# Revit family: NBS_Allermuir_OffcChrs-en-us-Cardita_SideChair
name_source: partatom
category: Furniture
revit_build: Autodesk Revit 2018 (Build: 20190510_1515(x64)
units: mm (PartAtom-declared; Revit-internal decimal feet)

## family parameters
Always vertical = Yes
Cut with Voids When Loaded = No
Room Calculation Point = No
Shared = No
Work Plane-Based = No

## types (1)
- Cardita_SideChair_CRD01
    AssetType = Movable
    BIMObjectName = NBS_Allermuir_OfficeChairs_Cardita_SideChair_CRD01-US
    Category = Pr_40_50_12_57:Office chairs
    ChairMaterial = NBS_Allermuir_Fabric
    Color = White as Snow, Back to Black, Slate Gray, Smoke Gray, Vintage Red, Ruby Red, Fern Green, Peacock Green
    Description = Side chair on wood legs
    DurationUnit = year
    ExpectedLife = 10
    Features = Molded shell, Fully upholstered with luxury quilt detail, Solid Ash legs with a clear finish, Plastic glides, Solid Ash legs can be stained or colorwashed, Plastic glides with felt
    Finish = White as Snow, Back to Black, Slate Gray, Smoke Gray, Vintage Red, Ruby Red, Fern Green, Peacock Green
    FrameFinish = Clear
    FrameMaterial = Solid Ash
    HighestSeatingHeight = 0 "
    IfcExportAs = IfcFurnitureType
    IfcExportType = CHAIR
    IsBuiltIn = No
    LegMaterial = NBS_Allermuir_Ash_ClearFinish
    LowestSeatingHeight = 0 "
    ManufacturerName = Allermuir
    ManufacturerURL = www.allermuir.com
    Material = Wood, steel
    ModelNumber = CRD01
    ModelReference = Cardita_SideChair
    NBSCertification = www.nationalbimlibrary.com/cert/rpltu2fz
    NBSDescription = Office chairs
    NBSReference = 45-35-20/330
    Name = OfficeChairs_CRD01_Cardita_Allermuir
    NominalDepth = 25 "
    NominalHeight = 33 "
    NominalLength = 22 "
    NominalWidth = 22 "
    OmniClassCode = 22-12 52 23
    OmniClassTitle = Office Seating
    OmniClassVersion = Table 22 2012-05-16
    ProductInformation = https://www.allermuir.com
    SeatDepth = 17.25"
    SeatWidth = 19"
    SeatingHeight = 17 "
    Size = 24.5 x 32.75 x 21.75"
    Status = UNSET
    Style = Chair
    SustainabilityPerformance = 99% recyclable
    Uniclass2015Code = Pr_40_50_12_57
    Uniclass2015Title = Office chairs
    Uniclass2015Version = Products v1.15
    Version = 1
    WarrantyDescription = Allermuir warrant that its manufactured products are free from manufacturing defects - in materials or workmanship - for a period of ten (10) years. , Allermuir will repair, or replace (at Allermuir's sole discretion) with comparable free of charge materials / components, any product / component which fails under normal use in a single shift environment, as a result of a defect in the materials and/ or workmanship
    WarrantyDurationParts = 10
    WarrantyDurationUnit = year
    WoodStains = White Oak, American Cherry, American Walnut, Dark walnut, Wenge

## geometry (parser evidence)
native form markers: Sweep x2
no freeform markers — native parametric forms only
